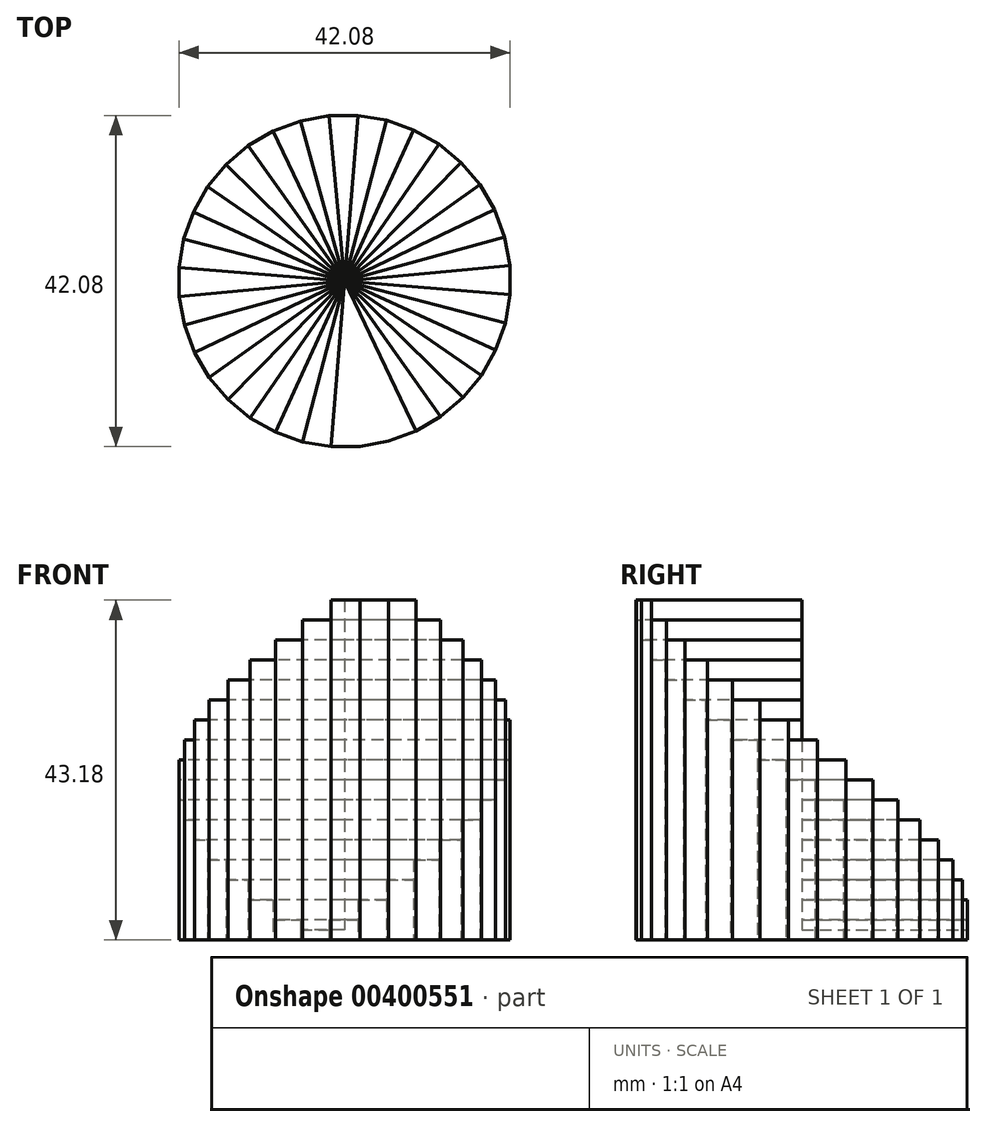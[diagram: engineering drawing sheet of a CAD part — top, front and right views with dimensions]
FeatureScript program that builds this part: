
annotation { "Feature Type Name" : "Feature", "Feature Type Description" : "" }
export const myFeature = defineFeature(function(context is Context, id is Id, definition is map)
    precondition{}
    {
        {
            var Q0;
            Q0=qCreatedBy(makeId("Top.planeOp"),FACE);
            var sketch = newSketch(context, id + "F0", { "sketchPlane" : qUnion([Q0])});
            skCircle(sketch, "E0.cCircle", {"center": v(0, 0) * mm, "radius": 21.02 * mm, "construction": true});
            skLineSegment(sketch, "E0.0", {"start": v(17.2, 12.23) * mm, "end": v(19.06, 9.06) * mm});
            skLineSegment(sketch, "E0.1", {"start": v(19.06, 9.06) * mm, "end": v(20.34, 5.6) * mm});
            skLineSegment(sketch, "E0.2", {"start": v(20.34, 5.6) * mm, "end": v(21, 2) * mm});
            skLineSegment(sketch, "E0.3", {"start": v(21, 2) * mm, "end": v(21.04, -1.69) * mm});
            skLineSegment(sketch, "E0.4", {"start": v(21.04, -1.69) * mm, "end": v(20.42, -5.32) * mm});
            skLineSegment(sketch, "E0.5", {"start": v(20.42, -5.32) * mm, "end": v(19.19, -8.78) * mm});
            skLineSegment(sketch, "E0.6", {"start": v(19.19, -8.78) * mm, "end": v(17.37, -11.98) * mm});
            skLineSegment(sketch, "E0.7", {"start": v(17.37, -11.98) * mm, "end": v(15.03, -14.81) * mm});
            skLineSegment(sketch, "E0.8", {"start": v(15.03, -14.81) * mm, "end": v(12.23, -17.2) * mm});
            skLineSegment(sketch, "E0.9", {"start": v(12.23, -17.2) * mm, "end": v(9.06, -19.06) * mm});
            skLineSegment(sketch, "E0.10", {"start": v(9.06, -19.06) * mm, "end": v(5.6, -20.34) * mm});
            skLineSegment(sketch, "E0.11", {"start": v(5.6, -20.34) * mm, "end": v(2, -21) * mm});
            skLineSegment(sketch, "E0.12", {"start": v(2, -21) * mm, "end": v(-1.69, -21.04) * mm});
            skLineSegment(sketch, "E0.13", {"start": v(-1.69, -21.04) * mm, "end": v(-5.32, -20.42) * mm});
            skLineSegment(sketch, "E0.14", {"start": v(-5.32, -20.42) * mm, "end": v(-8.78, -19.19) * mm});
            skLineSegment(sketch, "E0.15", {"start": v(-8.78, -19.19) * mm, "end": v(-11.98, -17.37) * mm});
            skLineSegment(sketch, "E0.16", {"start": v(-11.98, -17.37) * mm, "end": v(-14.81, -15.03) * mm});
            skLineSegment(sketch, "E0.17", {"start": v(-14.81, -15.03) * mm, "end": v(-17.2, -12.23) * mm});
            skLineSegment(sketch, "E0.18", {"start": v(-17.2, -12.23) * mm, "end": v(-19.06, -9.06) * mm});
            skLineSegment(sketch, "E0.19", {"start": v(-19.06, -9.06) * mm, "end": v(-20.34, -5.6) * mm});
            skLineSegment(sketch, "E0.20", {"start": v(-20.34, -5.6) * mm, "end": v(-21, -2) * mm});
            skLineSegment(sketch, "E0.21", {"start": v(-21, -2) * mm, "end": v(-21.04, 1.69) * mm});
            skLineSegment(sketch, "E0.22", {"start": v(-21.04, 1.69) * mm, "end": v(-20.42, 5.32) * mm});
            skLineSegment(sketch, "E0.23", {"start": v(-20.42, 5.32) * mm, "end": v(-19.19, 8.78) * mm});
            skLineSegment(sketch, "E0.24", {"start": v(-19.19, 8.78) * mm, "end": v(-17.37, 11.98) * mm});
            skLineSegment(sketch, "E0.25", {"start": v(-17.37, 11.98) * mm, "end": v(-15.03, 14.81) * mm});
            skLineSegment(sketch, "E0.26", {"start": v(-15.03, 14.81) * mm, "end": v(-12.23, 17.2) * mm});
            skLineSegment(sketch, "E0.27", {"start": v(-12.23, 17.2) * mm, "end": v(-9.06, 19.06) * mm});
            skLineSegment(sketch, "E0.28", {"start": v(-9.06, 19.06) * mm, "end": v(-5.6, 20.34) * mm});
            skLineSegment(sketch, "E0.29", {"start": v(-5.6, 20.34) * mm, "end": v(-2, 21) * mm});
            skLineSegment(sketch, "E0.30", {"start": v(-2, 21) * mm, "end": v(1.69, 21.04) * mm});
            skLineSegment(sketch, "E0.31", {"start": v(1.69, 21.04) * mm, "end": v(5.32, 20.42) * mm});
            skLineSegment(sketch, "E0.32", {"start": v(5.32, 20.42) * mm, "end": v(8.78, 19.19) * mm});
            skLineSegment(sketch, "E0.33", {"start": v(8.78, 19.19) * mm, "end": v(11.98, 17.37) * mm});
            skLineSegment(sketch, "E0.34", {"start": v(11.98, 17.37) * mm, "end": v(14.81, 15.03) * mm});
            skLineSegment(sketch, "E0.35", {"start": v(14.81, 15.03) * mm, "end": v(17.2, 12.23) * mm});
            skPoint(sketch, "E0.0.midPoint", {"position": v(18.13, 10.64) * mm});
            skLineSegment(sketch, "E1", {"start": v(1.69, 21.04) * mm, "end": v(-1.69, -21.04) * mm});
            skLineSegment(sketch, "E2", {"start": v(5.32, 20.42) * mm, "end": v(-5.32, -20.42) * mm});
            skLineSegment(sketch, "E3", {"start": v(8.78, 19.19) * mm, "end": v(-8.78, -19.19) * mm});
            skLineSegment(sketch, "E4", {"start": v(11.98, 17.37) * mm, "end": v(-11.98, -17.37) * mm});
            skLineSegment(sketch, "E5", {"start": v(14.81, 15.03) * mm, "end": v(-14.81, -15.03) * mm});
            skLineSegment(sketch, "E6", {"start": v(17.2, 12.23) * mm, "end": v(-17.2, -12.23) * mm});
            skLineSegment(sketch, "E7", {"start": v(19.06, 9.06) * mm, "end": v(-19.06, -9.06) * mm});
            skLineSegment(sketch, "E8", {"start": v(20.34, 5.6) * mm, "end": v(-20.34, -5.6) * mm});
            skLineSegment(sketch, "E9", {"start": v(21, 2) * mm, "end": v(-21, -2) * mm});
            skLineSegment(sketch, "E10", {"start": v(21.04, -1.69) * mm, "end": v(-21.04, 1.69) * mm});
            skLineSegment(sketch, "E11", {"start": v(20.42, -5.32) * mm, "end": v(-20.42, 5.32) * mm});
            skLineSegment(sketch, "E12", {"start": v(19.19, -8.78) * mm, "end": v(-19.19, 8.78) * mm});
            skLineSegment(sketch, "E13", {"start": v(17.37, -11.98) * mm, "end": v(-17.37, 11.98) * mm});
            skLineSegment(sketch, "E14", {"start": v(15.03, -14.81) * mm, "end": v(-15.03, 14.81) * mm});
            skLineSegment(sketch, "E15", {"start": v(12.23, -17.2) * mm, "end": v(-12.23, 17.2) * mm});
            skLineSegment(sketch, "E16", {"start": v(9.06, -19.06) * mm, "end": v(-9.06, 19.06) * mm});
            skLineSegment(sketch, "E17", {"start": v(5.6, -20.34) * mm, "end": v(-5.6, 20.34) * mm});
            skLineSegment(sketch, "E18", {"start": v(2, -21) * mm, "end": v(-2, 21) * mm});
            skSolve(sketch);
        }
        {
            var Q0;
            {var subQ0=sQuery(id+"F0.wireOp",EDGE,"E0.30");Q0=makeQuery(id+"F0.imprint","IMPRINT",FACE,{"disambiguationData":[TD([[makeQuery(id+"F0.imprint","IMPRINT",EDGE,{"derivedFrom":subQ0}),-1.0]])]});}
            extrude(context, id + "F1", {"entities" : qUnion([Q0]), "depth" : 2.54 * mm});
        }
        {
            var Q0;
            {var subQ0=sQuery(id+"F0.wireOp",EDGE,"E0.31");Q0=makeQuery(id+"F0.imprint","IMPRINT",FACE,{"disambiguationData":[TD([[makeQuery(id+"F0.imprint","IMPRINT",EDGE,{"derivedFrom":subQ0}),-1.0]])]});}
            extrude(context, id + "F2", {"entities" : qUnion([Q0]), "operationType" : NewBodyOperationType.ADD, "depth" : 5.08 * mm});
        }
        {
            var Q0;
            {var subQ0=sQuery(id+"F0.wireOp",EDGE,"E0.32");Q0=makeQuery(id+"F0.imprint","IMPRINT",FACE,{"disambiguationData":[TD([[makeQuery(id+"F0.imprint","IMPRINT",EDGE,{"derivedFrom":subQ0}),-1.0]])]});}
            extrude(context, id + "F3", {"entities" : qUnion([Q0]), "operationType" : NewBodyOperationType.ADD, "depth" : 7.62 * mm});
        }
        {
            var Q0;
            {var subQ0=sQuery(id+"F0.wireOp",EDGE,"E0.33");Q0=makeQuery(id+"F0.imprint","IMPRINT",FACE,{"disambiguationData":[TD([[makeQuery(id+"F0.imprint","IMPRINT",EDGE,{"derivedFrom":subQ0}),-1.0]])]});}
            extrude(context, id + "F4", {"entities" : qUnion([Q0]), "operationType" : NewBodyOperationType.ADD, "depth" : 10.16 * mm});
        }
        {
            var Q0;
            {var subQ0=sQuery(id+"F0.wireOp",EDGE,"E0.34");Q0=makeQuery(id+"F0.imprint","IMPRINT",FACE,{"disambiguationData":[TD([[makeQuery(id+"F0.imprint","IMPRINT",EDGE,{"derivedFrom":subQ0}),-1.0]])]});}
            extrude(context, id + "F5", {"entities" : qUnion([Q0]), "operationType" : NewBodyOperationType.ADD, "depth" : 12.7 * mm});
        }
        {
            var Q0;
            {var subQ0=sQuery(id+"F0.wireOp",EDGE,"E0.35");Q0=makeQuery(id+"F0.imprint","IMPRINT",FACE,{"disambiguationData":[TD([[makeQuery(id+"F0.imprint","IMPRINT",EDGE,{"derivedFrom":subQ0}),-1.0]])]});}
            extrude(context, id + "F6", {"entities" : qUnion([Q0]), "operationType" : NewBodyOperationType.ADD, "depth" : 15.24 * mm});
        }
        {
            var Q0;
            {var subQ0=sQuery(id+"F0.wireOp",EDGE,"E0.0");Q0=makeQuery(id+"F0.imprint","IMPRINT",FACE,{"disambiguationData":[TD([[makeQuery(id+"F0.imprint","IMPRINT",EDGE,{"derivedFrom":subQ0}),-1.0]])]});}
            extrude(context, id + "F7", {"entities" : qUnion([Q0]), "operationType" : NewBodyOperationType.ADD, "depth" : 17.78 * mm});
        }
        {
            var Q0;
            {var subQ0=sQuery(id+"F0.wireOp",EDGE,"E0.1");Q0=makeQuery(id+"F0.imprint","IMPRINT",FACE,{"disambiguationData":[TD([[makeQuery(id+"F0.imprint","IMPRINT",EDGE,{"derivedFrom":subQ0}),-1.0]])]});}
            extrude(context, id + "F8", {"entities" : qUnion([Q0]), "operationType" : NewBodyOperationType.ADD, "depth" : 20.32 * mm});
        }
        {
            var Q0;
            {var subQ0=sQuery(id+"F0.wireOp",EDGE,"E0.2");Q0=makeQuery(id+"F0.imprint","IMPRINT",FACE,{"disambiguationData":[TD([[makeQuery(id+"F0.imprint","IMPRINT",EDGE,{"derivedFrom":subQ0}),-1.0]])]});}
            extrude(context, id + "F9", {"entities" : qUnion([Q0]), "operationType" : NewBodyOperationType.ADD, "depth" : 22.86 * mm});
        }
        {
            var Q0;
            {var subQ0=sQuery(id+"F0.wireOp",EDGE,"E0.3");Q0=makeQuery(id+"F0.imprint","IMPRINT",FACE,{"disambiguationData":[TD([[makeQuery(id+"F0.imprint","IMPRINT",EDGE,{"derivedFrom":subQ0}),-1.0]])]});}
            extrude(context, id + "F10", {"entities" : qUnion([Q0]), "operationType" : NewBodyOperationType.ADD, "depth" : 25.4 * mm});
        }
        {
            var Q0;
            {var subQ0=sQuery(id+"F0.wireOp",EDGE,"E0.4");Q0=makeQuery(id+"F0.imprint","IMPRINT",FACE,{"disambiguationData":[TD([[makeQuery(id+"F0.imprint","IMPRINT",EDGE,{"derivedFrom":subQ0}),-1.0]])]});}
            extrude(context, id + "F11", {"entities" : qUnion([Q0]), "operationType" : NewBodyOperationType.ADD, "depth" : 27.94 * mm});
        }
        {
            var Q0;
            {var subQ0=sQuery(id+"F0.wireOp",EDGE,"E0.5");Q0=makeQuery(id+"F0.imprint","IMPRINT",FACE,{"disambiguationData":[TD([[makeQuery(id+"F0.imprint","IMPRINT",EDGE,{"derivedFrom":subQ0}),-1.0]])]});}
            extrude(context, id + "F12", {"entities" : qUnion([Q0]), "operationType" : NewBodyOperationType.ADD, "depth" : 30.48 * mm});
        }
        {
            var Q0;
            {var subQ0=sQuery(id+"F0.wireOp",EDGE,"E0.6");Q0=makeQuery(id+"F0.imprint","IMPRINT",FACE,{"disambiguationData":[TD([[makeQuery(id+"F0.imprint","IMPRINT",EDGE,{"derivedFrom":subQ0}),-1.0]])]});}
            extrude(context, id + "F13", {"entities" : qUnion([Q0]), "operationType" : NewBodyOperationType.ADD, "depth" : 33.02 * mm});
        }
        {
            var Q0;
            {var subQ0=sQuery(id+"F0.wireOp",EDGE,"E0.7");Q0=makeQuery(id+"F0.imprint","IMPRINT",FACE,{"disambiguationData":[TD([[makeQuery(id+"F0.imprint","IMPRINT",EDGE,{"derivedFrom":subQ0}),-1.0]])]});}
            extrude(context, id + "F14", {"entities" : qUnion([Q0]), "operationType" : NewBodyOperationType.ADD, "depth" : 35.56 * mm});
        }
        {
            var Q0;
            {var subQ0=sQuery(id+"F0.wireOp",EDGE,"E0.8");Q0=makeQuery(id+"F0.imprint","IMPRINT",FACE,{"disambiguationData":[TD([[makeQuery(id+"F0.imprint","IMPRINT",EDGE,{"derivedFrom":subQ0}),-1.0]])]});}
            extrude(context, id + "F15", {"entities" : qUnion([Q0]), "operationType" : NewBodyOperationType.ADD, "depth" : 38.1 * mm});
        }
        {
            var Q0;
            {var subQ0=sQuery(id+"F0.wireOp",EDGE,"E0.9");Q0=makeQuery(id+"F0.imprint","IMPRINT",FACE,{"disambiguationData":[TD([[makeQuery(id+"F0.imprint","IMPRINT",EDGE,{"derivedFrom":subQ0}),-1.0]])]});}
            extrude(context, id + "F16", {"entities" : qUnion([Q0]), "operationType" : NewBodyOperationType.ADD, "depth" : 40.64 * mm});
        }
        {
            var Q0;
            {var subQ0=sQuery(id+"F0.wireOp",EDGE,"E0.10");Q0=makeQuery(id+"F0.imprint","IMPRINT",FACE,{"disambiguationData":[TD([[makeQuery(id+"F0.imprint","IMPRINT",EDGE,{"derivedFrom":subQ0}),-1.0]])]});}
            extrude(context, id + "F17", {"entities" : qUnion([Q0]), "operationType" : NewBodyOperationType.ADD, "depth" : 43.18 * mm});
        }
        {
            var Q0;
            {var subQ0=sQuery(id+"F0.wireOp",EDGE,"E0.11");Q0=makeQuery(id+"F0.imprint","IMPRINT",FACE,{"disambiguationData":[TD([[makeQuery(id+"F0.imprint","IMPRINT",EDGE,{"derivedFrom":subQ0}),-1.0]])]});}
            extrude(context, id + "F18", {"entities" : qUnion([Q0]), "operationType" : NewBodyOperationType.ADD, "depth" : 43.18 * mm});
        }
        {
            var Q0;
            {var subQ0=sQuery(id+"F0.wireOp",EDGE,"E0.12");Q0=makeQuery(id+"F0.imprint","IMPRINT",FACE,{"disambiguationData":[TD([[makeQuery(id+"F0.imprint","IMPRINT",EDGE,{"derivedFrom":subQ0}),-1.0]])]});}
            extrude(context, id + "F19", {"entities" : qUnion([Q0]), "operationType" : NewBodyOperationType.ADD, "depth" : 43.18 * mm});
        }
        {
            var Q0;
            {var subQ0=sQuery(id+"F0.wireOp",EDGE,"E0.13");Q0=makeQuery(id+"F0.imprint","IMPRINT",FACE,{"disambiguationData":[TD([[makeQuery(id+"F0.imprint","IMPRINT",EDGE,{"derivedFrom":subQ0}),-1.0]])]});}
            extrude(context, id + "F20", {"entities" : qUnion([Q0]), "operationType" : NewBodyOperationType.ADD, "depth" : 40.64 * mm});
        }
        {
            var Q0;
            {var subQ0=sQuery(id+"F0.wireOp",EDGE,"E0.14");Q0=makeQuery(id+"F0.imprint","IMPRINT",FACE,{"disambiguationData":[TD([[makeQuery(id+"F0.imprint","IMPRINT",EDGE,{"derivedFrom":subQ0}),-1.0]])]});}
            extrude(context, id + "F21", {"entities" : qUnion([Q0]), "operationType" : NewBodyOperationType.ADD, "depth" : 38.1 * mm});
        }
        {
            var Q0;
            {var subQ0=sQuery(id+"F0.wireOp",EDGE,"E0.15");Q0=makeQuery(id+"F0.imprint","IMPRINT",FACE,{"disambiguationData":[TD([[makeQuery(id+"F0.imprint","IMPRINT",EDGE,{"derivedFrom":subQ0}),-1.0]])]});}
            extrude(context, id + "F22", {"entities" : qUnion([Q0]), "operationType" : NewBodyOperationType.ADD, "depth" : 35.56 * mm});
        }
        {
            var Q0;
            {var subQ0=sQuery(id+"F0.wireOp",EDGE,"E0.16");Q0=makeQuery(id+"F0.imprint","IMPRINT",FACE,{"disambiguationData":[TD([[makeQuery(id+"F0.imprint","IMPRINT",EDGE,{"derivedFrom":subQ0}),-1.0]])]});}
            extrude(context, id + "F23", {"entities" : qUnion([Q0]), "operationType" : NewBodyOperationType.ADD, "depth" : 33.02 * mm});
        }
        {
            var Q0;
            {var subQ0=sQuery(id+"F0.wireOp",EDGE,"E0.17");Q0=makeQuery(id+"F0.imprint","IMPRINT",FACE,{"disambiguationData":[TD([[makeQuery(id+"F0.imprint","IMPRINT",EDGE,{"derivedFrom":subQ0}),-1.0]])]});}
            extrude(context, id + "F24", {"entities" : qUnion([Q0]), "operationType" : NewBodyOperationType.ADD, "depth" : 30.48 * mm});
        }
        {
            var Q0;
            {var subQ0=sQuery(id+"F0.wireOp",EDGE,"E0.18");Q0=makeQuery(id+"F0.imprint","IMPRINT",FACE,{"disambiguationData":[TD([[makeQuery(id+"F0.imprint","IMPRINT",EDGE,{"derivedFrom":subQ0}),-1.0]])]});}
            extrude(context, id + "F25", {"entities" : qUnion([Q0]), "operationType" : NewBodyOperationType.ADD, "depth" : 27.94 * mm});
        }
        {
            var Q0;
            {var subQ0=sQuery(id+"F0.wireOp",EDGE,"E0.19");Q0=makeQuery(id+"F0.imprint","IMPRINT",FACE,{"disambiguationData":[TD([[makeQuery(id+"F0.imprint","IMPRINT",EDGE,{"derivedFrom":subQ0}),-1.0]])]});}
            extrude(context, id + "F26", {"entities" : qUnion([Q0]), "operationType" : NewBodyOperationType.ADD, "depth" : 25.4 * mm});
        }
        {
            var Q0;
            {var subQ0=sQuery(id+"F0.wireOp",EDGE,"E0.20");Q0=makeQuery(id+"F0.imprint","IMPRINT",FACE,{"disambiguationData":[TD([[makeQuery(id+"F0.imprint","IMPRINT",EDGE,{"derivedFrom":subQ0}),-1.0]])]});}
            extrude(context, id + "F27", {"entities" : qUnion([Q0]), "operationType" : NewBodyOperationType.ADD, "depth" : 22.86 * mm});
        }
        {
            var Q0;
            {var subQ0=sQuery(id+"F0.wireOp",EDGE,"E0.21");Q0=makeQuery(id+"F0.imprint","IMPRINT",FACE,{"disambiguationData":[TD([[makeQuery(id+"F0.imprint","IMPRINT",EDGE,{"derivedFrom":subQ0}),-1.0]])]});}
            extrude(context, id + "F28", {"entities" : qUnion([Q0]), "operationType" : NewBodyOperationType.ADD, "depth" : 20.32 * mm});
        }
        {
            var Q0;
            {var subQ0=sQuery(id+"F0.wireOp",EDGE,"E0.22");Q0=makeQuery(id+"F0.imprint","IMPRINT",FACE,{"disambiguationData":[TD([[makeQuery(id+"F0.imprint","IMPRINT",EDGE,{"derivedFrom":subQ0}),-1.0]])]});}
            extrude(context, id + "F29", {"entities" : qUnion([Q0]), "operationType" : NewBodyOperationType.ADD, "depth" : 17.78 * mm});
        }
        {
            var Q0;
            {var subQ0=sQuery(id+"F0.wireOp",EDGE,"E0.23");Q0=makeQuery(id+"F0.imprint","IMPRINT",FACE,{"disambiguationData":[TD([[makeQuery(id+"F0.imprint","IMPRINT",EDGE,{"derivedFrom":subQ0}),-1.0]])]});}
            extrude(context, id + "F30", {"entities" : qUnion([Q0]), "operationType" : NewBodyOperationType.ADD, "depth" : 15.24 * mm});
        }
        {
            var Q0;
            {var subQ0=sQuery(id+"F0.wireOp",EDGE,"E0.24");Q0=makeQuery(id+"F0.imprint","IMPRINT",FACE,{"disambiguationData":[TD([[makeQuery(id+"F0.imprint","IMPRINT",EDGE,{"derivedFrom":subQ0}),-1.0]])]});}
            extrude(context, id + "F31", {"entities" : qUnion([Q0]), "operationType" : NewBodyOperationType.ADD, "depth" : 12.7 * mm});
        }
        {
            var Q0;
            {var subQ0=sQuery(id+"F0.wireOp",EDGE,"E0.25");Q0=makeQuery(id+"F0.imprint","IMPRINT",FACE,{"disambiguationData":[TD([[makeQuery(id+"F0.imprint","IMPRINT",EDGE,{"derivedFrom":subQ0}),-1.0]])]});}
            extrude(context, id + "F32", {"entities" : qUnion([Q0]), "operationType" : NewBodyOperationType.ADD, "depth" : 10.16 * mm});
        }
        {
            var Q0;
            {var subQ0=sQuery(id+"F0.wireOp",EDGE,"E0.26");Q0=makeQuery(id+"F0.imprint","IMPRINT",FACE,{"disambiguationData":[TD([[makeQuery(id+"F0.imprint","IMPRINT",EDGE,{"derivedFrom":subQ0}),-1.0]])]});}
            extrude(context, id + "F33", {"entities" : qUnion([Q0]), "operationType" : NewBodyOperationType.ADD, "depth" : 7.62 * mm});
        }
        {
            var Q0;
            {var subQ0=sQuery(id+"F0.wireOp",EDGE,"E0.27");Q0=makeQuery(id+"F0.imprint","IMPRINT",FACE,{"disambiguationData":[TD([[makeQuery(id+"F0.imprint","IMPRINT",EDGE,{"derivedFrom":subQ0}),-1.0]])]});}
            extrude(context, id + "F34", {"entities" : qUnion([Q0]), "operationType" : NewBodyOperationType.ADD, "depth" : 5.08 * mm});
        }
        {
            var Q0;
            {var subQ0=sQuery(id+"F0.wireOp",EDGE,"E0.28");Q0=makeQuery(id+"F0.imprint","IMPRINT",FACE,{"disambiguationData":[TD([[makeQuery(id+"F0.imprint","IMPRINT",EDGE,{"derivedFrom":subQ0}),-1.0]])]});}
            extrude(context, id + "F35", {"entities" : qUnion([Q0]), "operationType" : NewBodyOperationType.ADD, "depth" : 2.54 * mm});
        }
        {
            var Q0;
            {var subQ0=sQuery(id+"F0.wireOp",EDGE,"E0.29");Q0=makeQuery(id+"F0.imprint","IMPRINT",FACE,{"disambiguationData":[TD([[makeQuery(id+"F0.imprint","IMPRINT",EDGE,{"derivedFrom":subQ0}),-1.0]])]});}
            extrude(context, id + "F36", {"entities" : qUnion([Q0]), "operationType" : NewBodyOperationType.ADD, "depth" : 1.27 * mm});
        }
    });
